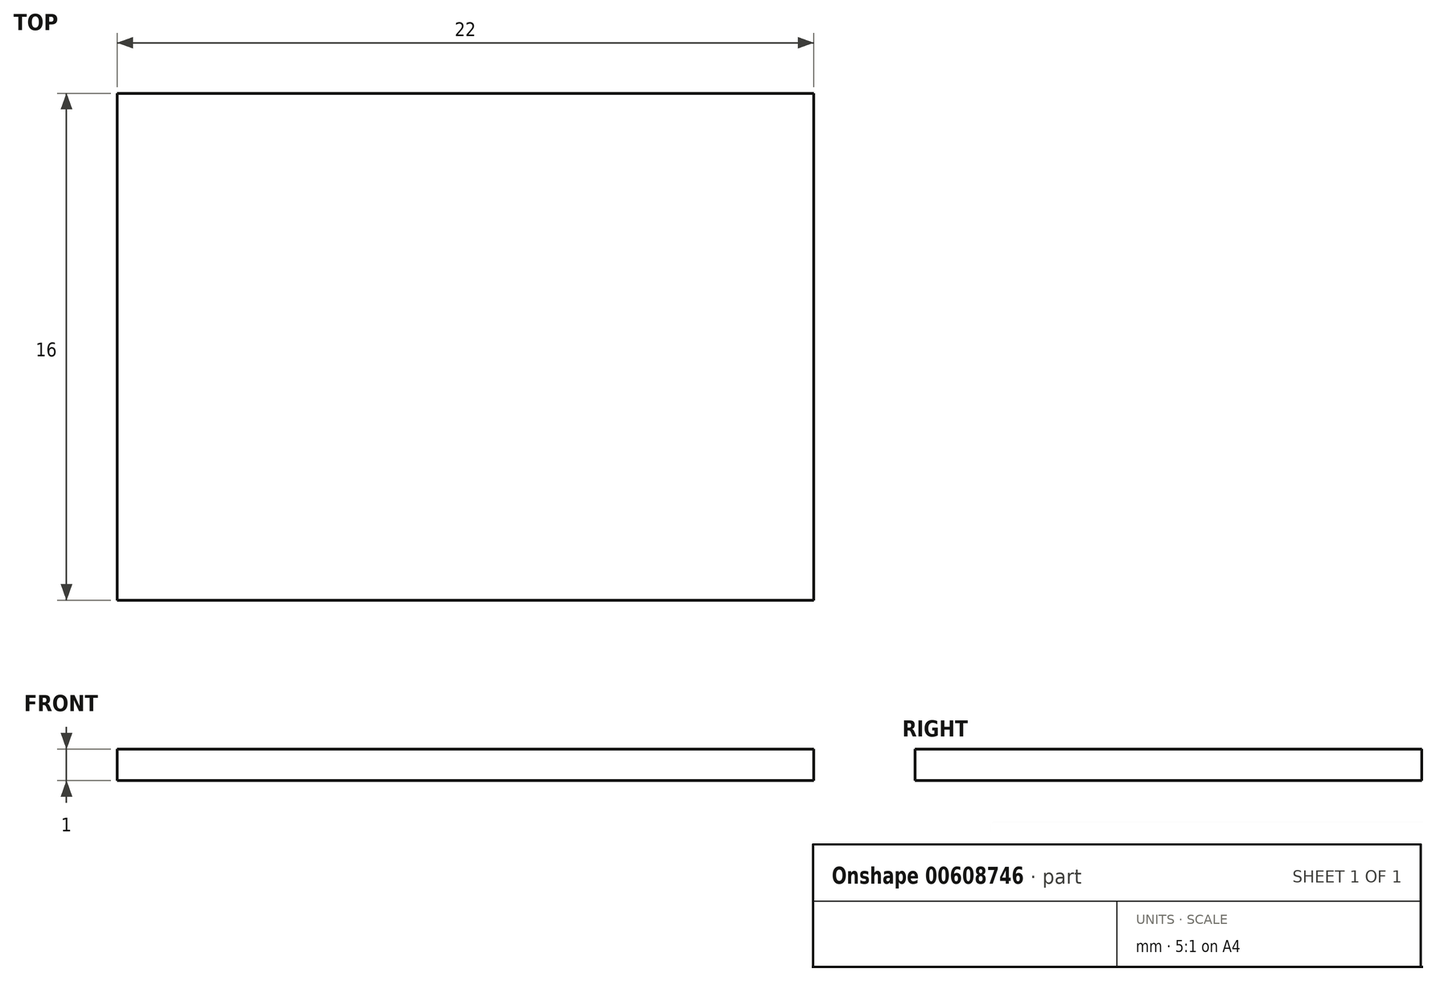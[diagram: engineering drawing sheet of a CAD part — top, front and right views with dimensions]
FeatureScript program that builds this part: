
annotation { "Feature Type Name" : "Feature", "Feature Type Description" : "" }
export const myFeature = defineFeature(function(context is Context, id is Id, definition is map)
    precondition{}
    {
        {
            var Q0;
            Q0=qCreatedBy(makeId("Top.planeOp"),FACE);
            var sketch = newSketch(context, id + "F0", { "sketchPlane" : qUnion([Q0])});
            skLineSegment(sketch, "E0.bottom", {"start": v(-11, 8) * mm, "end": v(11, 8) * mm});
            skLineSegment(sketch, "E0.top", {"start": v(-11, -8) * mm, "end": v(11, -8) * mm});
            skLineSegment(sketch, "E0.left", {"start": v(-11, 8) * mm, "end": v(-11, -8) * mm});
            skLineSegment(sketch, "E0.right", {"start": v(11, 8) * mm, "end": v(11, -8) * mm});
            skSolve(sketch);
        }
        {
            var Q0;
            Q0 = qSketchRegion(id + "F0", true);
            extrude(context, id + "F1", {"entities" : qUnion([Q0]), "depth" : 1 * mm, "offsetDistance" : 25 * mm});
        }
    });
